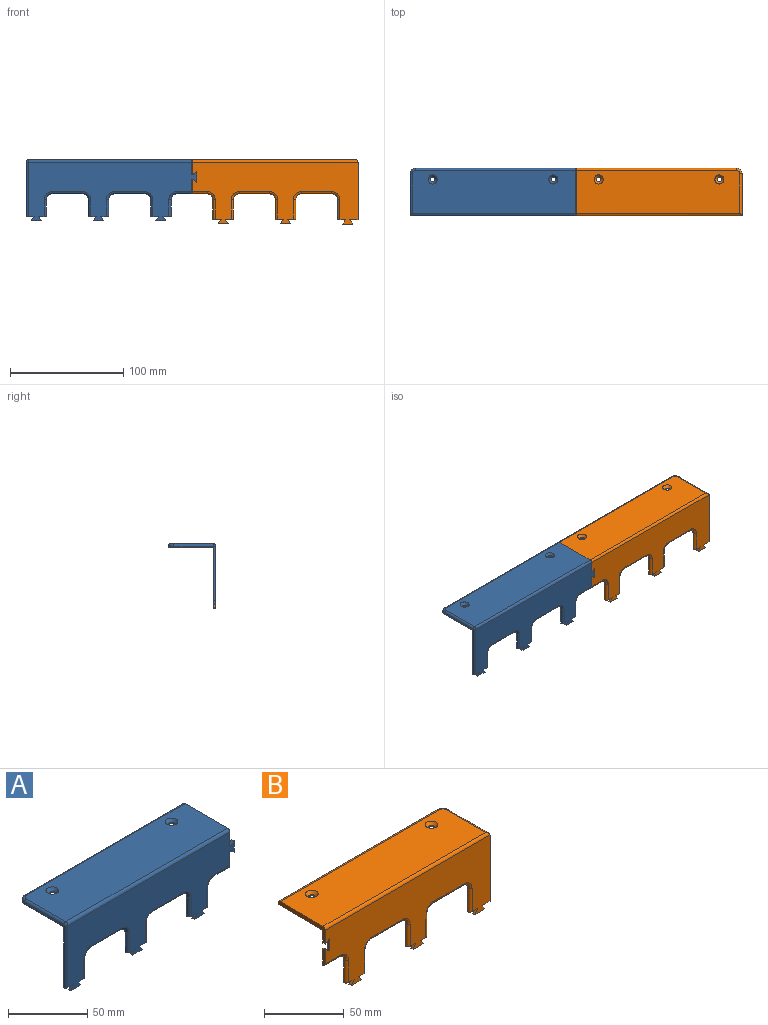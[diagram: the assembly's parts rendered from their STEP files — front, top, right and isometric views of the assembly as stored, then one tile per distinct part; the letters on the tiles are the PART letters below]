
ASSEMBLY  parts=2 mates=1
PART A: 50 faces, bbox 150.6x42.4x53.7 mm
  f0: plane 13.15x2mm, normal (1,0,0), area 25.4mm2, adj f19,f20,f22,f31
  f1: plane 3.7x2.59mm, normal (0.82,0,0.57), area 9mm2, adj f2,f18,f19,f20
  f2: plane 7.15x2mm, normal (0,0,-1), area 13.4mm2, adj f1,f19,f20,f43
  f3: plane 7.15x2mm, normal (0,0,-1), area 13.4mm2, adj f4,f19,f20,f39
  f4: plane 3.7x2.59mm, normal (-0.82,0,0.57), area 9mm2, adj f3,f5,f19,f20
  f5: plane 8.88x2mm, normal (0,0,-1), area 17.8mm2, adj f4,f6,f19,f20
  f6: plane 3.7x2.59mm, normal (0.82,0,0.57), area 9mm2, adj f5,f7,f19,f20
  f7: plane 7.15x2mm, normal (0,0,-1), area 13.4mm2, adj f6,f19,f20,f38
  f8: plane 7.15x2mm, normal (0,0,-1), area 13.4mm2, adj f9,f19,f20,f34
  f9: plane 3.7x2.59mm, normal (-0.82,0,0.57), area 9mm2, adj f8,f10,f19,f20
  f10: plane 8.88x2mm, normal (0,0,-1), area 17.8mm2, adj f9,f11,f19,f20
  f11: plane 3.7x2.59mm, normal (0.82,0,0.57), area 9mm2, adj f10,f12,f19,f20
  f12: plane 7.15x2mm, normal (0,0,-1), area 13.4mm2, adj f11,f19,f20,f33
  f13: plane 42x13.15mm, normal (1,0,0), area 144.6mm2, adj f14,f19,f20,f21,f24,f25,f44,f46
  f14: plane 144.5x38mm, normal (0,0,1), area 5388.5mm2, adj f13,f28,f29,f44,f46,f48,f49
  f15: plane 35x1mm, normal (-1,0,0), area 35mm2, adj f24,f30,f45,f49
  f16: plane 7.15x2mm, normal (0,0,-1), area 13.4mm2, adj f17,f19,f20,f45
  f17: plane 3.7x2.59mm, normal (-0.82,0,0.57), area 9mm2, adj f16,f18,f19,f20
  f18: plane 8.88x2mm, normal (0,0,-1), area 17.8mm2, adj f1,f17,f19,f20
  f19: plane 148.2x51.7mm, normal (0,-1,0), area 4826.7mm2, adj f0,f1,f2,f3,f4,f5,f6,f7
  f20: plane 150.2x50.7mm, normal (0,1,0), area 5155.4mm2, adj f0,f1,f2,f3,f4,f5,f6,f7
  f21: plane 3.7x2.59mm, normal (-0.57,0,0.82), area 9mm2, adj f13,f19,f20,f23
  f22: plane 3.7x2.59mm, normal (-0.57,0,-0.82), area 9mm2, adj f0,f19,f20,f23
  f23: plane 8.88x2mm, normal (1,0,0), area 17.8mm2, adj f19,f20,f21,f22
  f24: plane 146.5x40mm, normal (0,0,-1), area 5829.5mm2, adj f13,f15,f20,f25,f26,f27,f30
  f25: plane 141.5x1mm, normal (0,1,0), area 141.5mm2, adj f13,f24,f30,f46
  f26: cylinder r=2mm len=4mm, axis (0,0,1), area 12.6mm2, adj f24,f28
  f27: cylinder r=2mm len=4mm, axis (0,0,1), area 12.6mm2, adj f24,f29
  f28: cone r=2mm half-angle=45deg, axis (0,0,1), area 53.3mm2, adj f14,f26
  f29: cone r=2mm half-angle=45deg, axis (0,0,1), area 53.3mm2, adj f14,f27
  f30: cylinder r=5mm len=5mm, axis (0,0,1), area 7.9mm2, adj f15,f24,f25,f48
  f31: cylinder r=2mm len=13.5mm, axis (-1,0,0), area 42.4mm2, adj f0,f19,f20,f32
  f32: torus R=7mm, axis (0,-1,0), area 28.3mm2, adj f19,f20,f31,f33
  f33: cylinder r=2mm len=15mm, axis (0,0,-1), area 47.1mm2, adj f12,f19,f20,f32
  f34: cylinder r=2mm len=15mm, axis (0,0,1), area 47.1mm2, adj f8,f19,f20,f35
  f35: torus R=7mm, axis (0,-1,0), area 28.3mm2, adj f19,f20,f34,f36
  f36: cylinder r=2mm len=27mm, axis (-1,0,0), area 84.8mm2, adj f19,f20,f35,f37
  f37: torus R=7mm, axis (0,-1,0), area 28.3mm2, adj f19,f20,f36,f38
  f38: cylinder r=2mm len=15mm, axis (0,0,-1), area 47.1mm2, adj f7,f19,f20,f37
  f39: cylinder r=2mm len=15mm, axis (0,0,1), area 47.1mm2, adj f3,f19,f20,f40
  f40: torus R=7mm, axis (0,-1,0), area 28.3mm2, adj f19,f20,f39,f41
  f41: cylinder r=2mm len=27mm, axis (-1,0,0), area 84.8mm2, adj f19,f20,f40,f42
  f42: torus R=7mm, axis (0,-1,0), area 28.3mm2, adj f19,f20,f41,f43
  f43: cylinder r=2mm len=15mm, axis (0,0,-1), area 47.1mm2, adj f2,f19,f20,f42
  f44: cylinder r=2mm len=144.5mm, axis (1,0,0), area 454mm2, adj f13,f14,f19,f47
  f45: cylinder r=2mm len=48mm, axis (0,0,1), area 150.8mm2, adj f15,f16,f19,f20,f47
  f46: cylinder r=2mm len=141.5mm, axis (1,0,0), area 444.5mm2, adj f13,f14,f25,f48
  f47: sphere r=2mm, area 6.3mm2, adj f44,f45,f49
  f48: torus R=3mm, axis (0,0,1), area 21.1mm2, adj f14,f30,f46,f49
  f49: cylinder r=2mm len=35mm, axis (0,-1,0), area 110mm2, adj f14,f15,f47,f48
PART B: 48 faces, bbox 146.9x42.4x56.6 mm
  f0: plane 146.5x53.61mm, normal (0,1,0), area 5243.4mm2, adj f1,f2,f3,f4,f5,f6,f7,f8
  f1: plane 42x13mm, normal (-1,0,0), area 144.3mm2, adj f0,f15,f20,f21,f24,f25,f41,f42
  f2: plane 3.7x2.59mm, normal (0.82,0,0.57), area 9mm2, adj f0,f3,f19,f20
  f3: plane 7.15x2mm, normal (0,0,-1), area 13.4mm2, adj f0,f2,f20,f40
  f4: plane 7.15x2mm, normal (0,0,-1), area 13.4mm2, adj f0,f5,f20,f36
  f5: plane 3.7x2.59mm, normal (-0.82,0,0.57), area 9mm2, adj f0,f4,f6,f20
  f6: plane 8.88x2mm, normal (0,0,-1), area 17.8mm2, adj f0,f5,f7,f20
  f7: plane 3.7x2.59mm, normal (0.82,0,0.57), area 9mm2, adj f0,f6,f8,f20
  f8: plane 7.15x2mm, normal (0,0,-1), area 13.4mm2, adj f0,f7,f20,f35
  f9: plane 7.15x2mm, normal (0,0,-1), area 13.4mm2, adj f0,f10,f20,f31
  f10: plane 3.7x2.59mm, normal (-0.82,0,0.57), area 9mm2, adj f0,f9,f11,f20
  f11: plane 8.88x2mm, normal (0,0,-1), area 17.8mm2, adj f0,f10,f12,f20
  f12: plane 3.7x2.59mm, normal (0.82,0,0.57), area 9mm2, adj f0,f11,f13,f20
  f13: plane 7.15x2mm, normal (0,0,-1), area 14.3mm2, adj f0,f12,f14,f20
  f14: plane 50.91x37mm, normal (1,0,0), area 136.8mm2, adj f0,f13,f20,f24,f30,f44
  f15: plane 144.5x38mm, normal (0,0,1), area 5388.5mm2, adj f1,f28,f29,f41,f42,f43,f44
  f16: plane 13x2mm, normal (-1,0,0), area 25.1mm2, adj f0,f20,f23,f47
  f17: plane 7.15x2mm, normal (0,0,-1), area 13.4mm2, adj f0,f18,f20,f45
  f18: plane 3.7x2.59mm, normal (-0.82,0,0.57), area 9mm2, adj f0,f17,f19,f20
  f19: plane 8.88x2mm, normal (0,0,-1), area 17.8mm2, adj f0,f2,f18,f20
  f20: plane 146.5x54.61mm, normal (0,-1,0), area 4985.7mm2, adj f1,f2,f3,f4,f5,f6,f7,f8
  f21: plane 4x2.8mm, normal (0.57,0,-0.82), area 9.8mm2, adj f0,f1,f20,f22
  f22: plane 9.6x2mm, normal (-1,0,0), area 19.2mm2, adj f0,f20,f21,f23
  f23: plane 4x2.8mm, normal (0.57,0,0.82), area 9.8mm2, adj f0,f16,f20,f22
  f24: plane 146.5x40mm, normal (0,0,-1), area 5829.5mm2, adj f0,f1,f14,f25,f26,f27,f30
  f25: plane 141.5x1mm, normal (0,1,0), area 141.5mm2, adj f1,f24,f30,f41
  f26: cylinder r=2mm len=4mm, axis (0,0,1), area 12.6mm2, adj f24,f28
  f27: cylinder r=2mm len=4mm, axis (0,0,1), area 12.6mm2, adj f24,f29
  f28: cone r=2mm half-angle=45deg, axis (0,0,1), area 53.3mm2, adj f15,f26
  f29: cone r=2mm half-angle=45deg, axis (0,0,1), area 53.3mm2, adj f15,f27
  f30: cylinder r=5mm len=5mm, axis (0,0,-1), area 7.9mm2, adj f14,f24,f25,f43
  f31: cylinder r=2mm len=17.91mm, axis (0,0,1), area 56.3mm2, adj f0,f9,f20,f32
  f32: torus R=7mm, axis (0,-1,0), area 28.3mm2, adj f0,f20,f31,f33
  f33: cylinder r=2mm len=27mm, axis (-1,0,0), area 84.8mm2, adj f0,f20,f32,f34
  f34: torus R=7mm, axis (0,-1,0), area 28.3mm2, adj f0,f20,f33,f35
  f35: cylinder r=2mm len=17.25mm, axis (0,0,-1), area 54.2mm2, adj f0,f8,f20,f34
  f36: cylinder r=2mm len=17.25mm, axis (0,0,1), area 54.2mm2, adj f0,f4,f20,f37
  f37: torus R=7mm, axis (0,-1,0), area 28.3mm2, adj f0,f20,f36,f38
  f38: cylinder r=2mm len=27mm, axis (-1,0,0), area 84.8mm2, adj f0,f20,f37,f39
  f39: torus R=7mm, axis (0,-1,0), area 28.3mm2, adj f0,f20,f38,f40
  f40: cylinder r=2mm len=17.53mm, axis (0,0,-1), area 55.1mm2, adj f0,f3,f20,f39
  f41: cylinder r=2mm len=141.5mm, axis (1,0,0), area 444.5mm2, adj f1,f15,f25,f43
  f42: cylinder r=2mm len=146.5mm, axis (1,0,0), area 458mm2, adj f1,f15,f20,f44
  f43: torus R=3mm, axis (0,0,1), area 21.1mm2, adj f15,f30,f41,f44
  f44: cylinder r=2mm len=37mm, axis (0,1,0), area 114mm2, adj f14,f15,f42,f43
  f45: cylinder r=2mm len=17.53mm, axis (0,0,1), area 55.1mm2, adj f0,f17,f20,f46
  f46: torus R=7mm, axis (0,-1,0), area 28.3mm2, adj f0,f20,f45,f47
  f47: cylinder r=2mm len=13.5mm, axis (-1,0,0), area 42.4mm2, adj f0,f16,f20,f46
PLACE A at identity
PLACE B t=(-34.73,0,0)mm
MATE fastened B.f16 <-> A.f0  axis (-1,0,0) through (53.14,0,39.57)mm
